# Revit family: Kessel 28799 en
name_source: partatom
category: Sanitärinstallationen
revit_build: Autodesk Revit 2017 (Build: 20160225_1515(x64)
units: mm (PartAtom-declared; Revit-internal decimal feet)

## family parameters
Arbeitsebenenbasiert = Nein
Beim Laden mit Abzugskörper schneiden = Nein
Bemaßung runder Anschluss = Durchmesser verwenden
Gemeinsam genutzt = Nein
Immer vertikal = Ja
Raumberechnungspunkt = Nein
Teiletyp = Normal

## types (1)
- Kessel 28799 en
    <1.010.00.2> Number of the part of the guideline = 4
    <1.010.00.3> Issue date (month) of the guideline = 201410
    <1.010.00.4> Manufacturer name = Kessel
    <1.010.00.5> Revision date of the file = 20190228
    <1.800.00.3> BS number = 10000100000000000000000000000000000000000000000126000
    <1.800.00.4> Comment field = Klemmdose für Verlängerung Pegelsonde
    <1.810.00.3> Manufacturer’s reference number = 28799
    <1.810.00.4> DATANORM number = 28799
    <1.960/3L.00.8> Link (URL) = http://www.kessel.de
    <4.100.00.4> Area of application = Zubehör
    <4.110.00.4> Model series = Zubehör
    <4.700.00.10> Star / delta starting circuit with three-phase connection or three-phase current = no
    <4.700.00.46> vertical installation = no
    <4.700.00.47> outdoor installation = no
    <4.700.00.48> ATEX = no
    <4.700.00.49> protection class = protection class I
    <4.700.00.4> Product name = Klemmdose für Verlängerung Pegelsonde
    <4.700.00.50> motor protection = no
    CONNECTOR0_DIAMETER_dZ_0r = 0 mm  [stored 0 ft]
    CONNECTOR0_dZ_00 = 9 mm  [stored 0.0295276 ft]
    CONNECTOR0_dZ_01 = 2 mm  [stored 0.00656168 ft]
    CONNECTOR0_ref_dY = 13 mm
    CONNECTOR0_ref_dZ = 2 mm  [stored 0.00656168 ft]
    CONNECTOR1_DIAMETER_dZ_0r = 0 mm  [stored 0 ft]
    CONNECTOR1_dZ_00 = 25 mm  [stored 0.082021 ft]
    CONNECTOR1_dZ_01 = 10 mm  [stored 0.0328084 ft]
    CONNECTOR1_ref_dX = 19 mm
    CONNECTOR1_ref_dY = 27 mm
    CONNECTOR1_ref_dZ = 10 mm  [stored 0.0328084 ft]
    CONNECTOR2_DIAMETER_dZ_0r = 0 mm  [stored 0 ft]
    CONNECTOR2_dZ_00 = 25 mm  [stored 0.082021 ft]
    CONNECTOR2_dZ_01 = 10 mm  [stored 0.0328084 ft]
    CONNECTOR2_ref_dX = 19 mm
    CONNECTOR2_ref_dY = 27 mm
    CONNECTOR2_ref_dZ = 10 mm  [stored 0.0328084 ft]
    Hersteller = Kessel
    Modell = 28799
    URL = www.kessel.de

note: [stored X ft] marks values corroborated as IEEE doubles in the binary element streams (Revit-internal decimal feet)

## geometry (parser evidence)
native form markers: Sweep x2
no freeform markers — native parametric forms only
